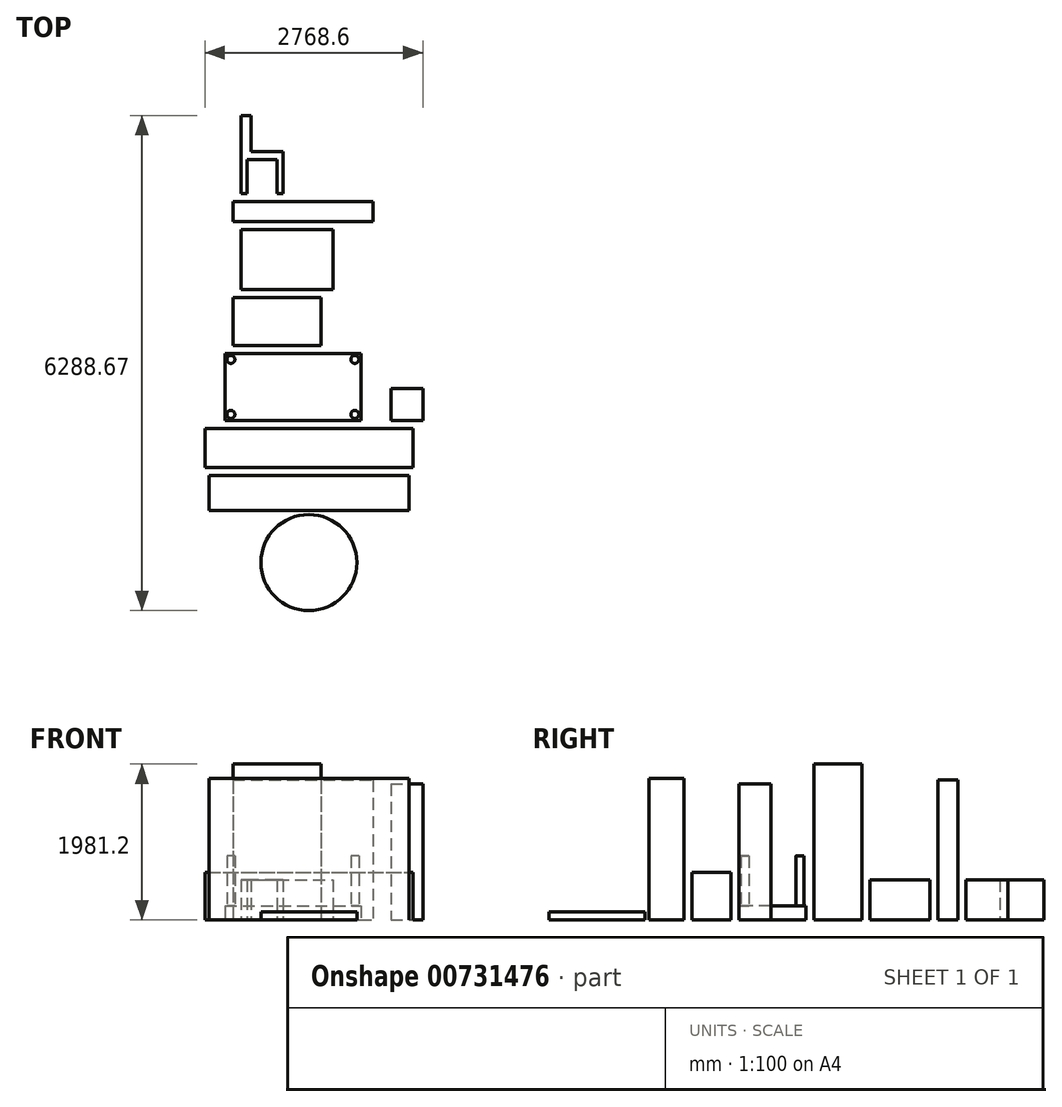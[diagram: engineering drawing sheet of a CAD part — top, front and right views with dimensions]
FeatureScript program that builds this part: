
annotation { "Feature Type Name" : "Feature", "Feature Type Description" : "" }
export const myFeature = defineFeature(function(context is Context, id is Id, definition is map)
    precondition{}
    {
        {
            var Q0;
            Q0=qCreatedBy(makeId("Top.planeOp"),FACE);
            var sketch = newSketch(context, id + "F0", { "sketchPlane" : qUnion([Q0])});
            skLineSegment(sketch, "E0.bottom", {"start": v(-1320.8, 50.8) * mm, "end": v(1320.8, 50.8) * mm});
            skLineSegment(sketch, "E0.top", {"start": v(-1320.8, 546.1) * mm, "end": v(1320.8, 546.1) * mm});
            skLineSegment(sketch, "E0.left", {"start": v(-1320.8, 50.8) * mm, "end": v(-1320.8, 546.1) * mm});
            skLineSegment(sketch, "E0.right", {"start": v(1320.8, 50.8) * mm, "end": v(1320.8, 546.1) * mm});
            skLineSegment(sketch, "E1.bottom", {"start": v(-1270, -50.8) * mm, "end": v(1270, -50.8) * mm});
            skLineSegment(sketch, "E1.top", {"start": v(-1270, -495.3) * mm, "end": v(1270, -495.3) * mm});
            skLineSegment(sketch, "E1.left", {"start": v(-1270, -50.8) * mm, "end": v(-1270, -495.3) * mm});
            skLineSegment(sketch, "E1.right", {"start": v(1270, -50.8) * mm, "end": v(1270, -495.3) * mm});
            skLineSegment(sketch, "E2", {"start": v(0, 50.8) * mm, "end": v(0, -50.8) * mm});
            skLineSegment(sketch, "E3.bottom", {"start": v(-1066.8, 1498.6) * mm, "end": v(660.4, 1498.6) * mm});
            skLineSegment(sketch, "E3.top", {"start": v(-1066.8, 647.7) * mm, "end": v(660.4, 647.7) * mm});
            skLineSegment(sketch, "E3.left", {"start": v(-1066.8, 1498.6) * mm, "end": v(-1066.8, 647.7) * mm});
            skLineSegment(sketch, "E3.right", {"start": v(660.4, 1498.6) * mm, "end": v(660.4, 647.7) * mm});
            skCircle(sketch, "E4", {"center": v(-990.6, 723.9) * mm, "radius": 50.8 * mm});
            skCircle(sketch, "E5", {"center": v(-990.6, 1422.4) * mm, "radius": 50.8 * mm});
            skCircle(sketch, "E6", {"center": v(584.2, 1422.4) * mm, "radius": 50.8 * mm});
            skCircle(sketch, "E7", {"center": v(584.2, 723.9) * mm, "radius": 50.8 * mm});
            skLineSegment(sketch, "E8.0", {"start": v(-990.6, 1422.4) * mm, "end": v(584.2, 1422.4) * mm, "construction": true});
            skLineSegment(sketch, "E8.1", {"start": v(-990.6, 1422.4) * mm, "end": v(-990.6, 723.9) * mm, "construction": true});
            skLineSegment(sketch, "E8.2", {"start": v(-990.6, 723.9) * mm, "end": v(584.2, 723.9) * mm, "construction": true});
            skLineSegment(sketch, "E8.3", {"start": v(584.2, 1422.4) * mm, "end": v(584.2, 723.9) * mm, "construction": true});
            skLineSegment(sketch, "E9.bottom", {"start": v(-965.2, 1600.2) * mm, "end": v(152.4, 1600.2) * mm});
            skLineSegment(sketch, "E9.top", {"start": v(-965.2, 2209.8) * mm, "end": v(152.4, 2209.8) * mm});
            skLineSegment(sketch, "E9.left", {"start": v(-965.2, 1600.2) * mm, "end": v(-965.2, 2209.8) * mm});
            skLineSegment(sketch, "E9.right", {"start": v(152.4, 1600.2) * mm, "end": v(152.4, 2209.8) * mm});
            skLineSegment(sketch, "E10.bottom", {"start": v(-863.6, 2311.4) * mm, "end": v(304.8, 2311.4) * mm});
            skLineSegment(sketch, "E10.top", {"start": v(-863.6, 3073.4) * mm, "end": v(304.8, 3073.4) * mm});
            skLineSegment(sketch, "E10.left", {"start": v(-863.6, 2311.4) * mm, "end": v(-863.6, 3073.4) * mm});
            skLineSegment(sketch, "E10.right", {"start": v(304.8, 2311.4) * mm, "end": v(304.8, 3073.4) * mm});
            skLineSegment(sketch, "E11.bottom", {"start": v(-965.2, 3175) * mm, "end": v(812.8, 3175) * mm});
            skLineSegment(sketch, "E11.top", {"start": v(-965.2, 3429) * mm, "end": v(812.8, 3429) * mm});
            skLineSegment(sketch, "E11.left", {"start": v(-965.2, 3175) * mm, "end": v(-965.2, 3429) * mm});
            skLineSegment(sketch, "E11.right", {"start": v(812.8, 3175) * mm, "end": v(812.8, 3429) * mm});
            skLineSegment(sketch, "E12", {"start": v(-863.6, 3530.6) * mm, "end": v(-863.6, 4521.2) * mm});
            skLineSegment(sketch, "E13", {"start": v(-863.6, 4521.2) * mm, "end": v(-736.6, 4521.2) * mm});
            skLineSegment(sketch, "E14", {"start": v(-736.6, 4521.2) * mm, "end": v(-736.6, 4064) * mm});
            skLineSegment(sketch, "E15", {"start": v(-736.6, 4064) * mm, "end": v(-330.2, 4064) * mm});
            skLineSegment(sketch, "E16", {"start": v(-330.2, 4064) * mm, "end": v(-330.2, 3530.6) * mm});
            skLineSegment(sketch, "E17", {"start": v(-330.2, 3530.6) * mm, "end": v(-406.4, 3530.6) * mm});
            skLineSegment(sketch, "E18", {"start": v(-406.4, 3530.6) * mm, "end": v(-406.4, 3962.4) * mm});
            skLineSegment(sketch, "E19", {"start": v(-406.4, 3962.4) * mm, "end": v(-787.4, 3962.4) * mm});
            skLineSegment(sketch, "E20", {"start": v(-787.4, 3962.4) * mm, "end": v(-787.4, 3530.6) * mm});
            skLineSegment(sketch, "E21", {"start": v(-787.4, 3530.6) * mm, "end": v(-863.6, 3530.6) * mm});
            skLineSegment(sketch, "E22.bottom", {"start": v(1041.4, 647.7) * mm, "end": v(1447.8, 647.7) * mm});
            skLineSegment(sketch, "E22.top", {"start": v(1041.4, 1054.1) * mm, "end": v(1447.8, 1054.1) * mm});
            skLineSegment(sketch, "E22.left", {"start": v(1041.4, 647.7) * mm, "end": v(1041.4, 1054.1) * mm});
            skLineSegment(sketch, "E22.right", {"start": v(1447.8, 647.7) * mm, "end": v(1447.8, 1054.1) * mm});
            skCircle(sketch, "E23", {"center": v(0, -1157.87) * mm, "radius": 609.6 * mm});
            skSolve(sketch);
        }
        {
            var Q0;
            Q0=makeQuery(id+"F0.imprint","IMPRINT",FACE,{"disambiguationData":[TD([[makeQuery(id+"F0.imprint","IMPRINT",EDGE,{"derivedFrom":sQuery(id+"F0.wireOp",EDGE,"E0.top")}),-1.0]])]});
            extrude(context, id + "F1", {"entities" : qUnion([Q0]), "depth" : 603.25 * mm, "offsetDistance" : 25.4 * mm});
        }
        {
            var Q0;
            Q0=makeQuery(id+"F0.imprint","IMPRINT",FACE,{"disambiguationData":[TD([[makeQuery(id+"F0.imprint","IMPRINT",EDGE,{"derivedFrom":sQuery(id+"F0.wireOp",EDGE,"E1.top")}),1.0]])]});
            extrude(context, id + "F2", {"entities" : qUnion([Q0]), "depth" : 1797.05 * mm, "offsetDistance" : 25.4 * mm});
        }
        {
            var Q0;
            Q0=makeQuery(id+"F0.imprint","IMPRINT",FACE,{"disambiguationData":[TD([[makeQuery(id+"F0.imprint","IMPRINT",EDGE,{"derivedFrom":sQuery(id+"F0.wireOp",EDGE,"E3.bottom")}),-1.0]])]});
            extrude(context, id + "F3", {"entities" : qUnion([Q0]), "depth" : 177.8 * mm, "offsetDistance" : 25.4 * mm});
        }
        {
            var Q0;
            Q0=makeQuery(id+"F0.imprint","IMPRINT",FACE,{"disambiguationData":[TD([[makeQuery(id+"F0.imprint","IMPRINT",EDGE,{"derivedFrom":sQuery(id+"F0.wireOp",EDGE,"E5")}),1.0]])]});
            var Q1;
            Q1=makeQuery(id+"F0.imprint","IMPRINT",FACE,{"disambiguationData":[TD([[makeQuery(id+"F0.imprint","IMPRINT",EDGE,{"derivedFrom":sQuery(id+"F0.wireOp",EDGE,"E6")}),1.0]])]});
            var Q2;
            Q2=makeQuery(id+"F0.imprint","IMPRINT",FACE,{"disambiguationData":[TD([[makeQuery(id+"F0.imprint","IMPRINT",EDGE,{"derivedFrom":sQuery(id+"F0.wireOp",EDGE,"E4")}),1.0]])]});
            var Q3;
            Q3=makeQuery(id+"F0.imprint","IMPRINT",FACE,{"disambiguationData":[TD([[makeQuery(id+"F0.imprint","IMPRINT",EDGE,{"derivedFrom":sQuery(id+"F0.wireOp",EDGE,"E7")}),1.0]])]});
            extrude(context, id + "F4", {"entities" : qUnion([Q0, Q1, Q2, Q3]), "operationType" : NewBodyOperationType.ADD, "depth" : 812.8 * mm, "offsetDistance" : 25.4 * mm});
        }
        {
            var Q0;
            Q0=makeQuery(id+"F0.imprint","IMPRINT",FACE,{"disambiguationData":[TD([[makeQuery(id+"F0.imprint","IMPRINT",EDGE,{"derivedFrom":sQuery(id+"F0.wireOp",EDGE,"E9.bottom")}),1.0]])]});
            extrude(context, id + "F5", {"entities" : qUnion([Q0]), "depth" : 1981.2 * mm, "offsetDistance" : 25.4 * mm});
        }
        {
            var Q0;
            Q0=makeQuery(id+"F0.imprint","IMPRINT",FACE,{"disambiguationData":[TD([[makeQuery(id+"F0.imprint","IMPRINT",EDGE,{"derivedFrom":sQuery(id+"F0.wireOp",EDGE,"E10.bottom")}),1.0]])]});
            extrude(context, id + "F6", {"entities" : qUnion([Q0]), "depth" : 508 * mm, "offsetDistance" : 25.4 * mm});
        }
        {
            var Q0;
            Q0=makeQuery(id+"F0.imprint","IMPRINT",FACE,{"disambiguationData":[TD([[makeQuery(id+"F0.imprint","IMPRINT",EDGE,{"derivedFrom":sQuery(id+"F0.wireOp",EDGE,"E11.bottom")}),1.0]])]});
            extrude(context, id + "F7", {"entities" : qUnion([Q0]), "depth" : 1778 * mm, "offsetDistance" : 25.4 * mm});
        }
        {
            var Q0;
            Q0=makeQuery(id+"F0.imprint","IMPRINT",FACE,{"disambiguationData":[TD([[makeQuery(id+"F0.imprint","IMPRINT",EDGE,{"derivedFrom":sQuery(id+"F0.wireOp",EDGE,"E12")}),-1.0]])]});
            extrude(context, id + "F8", {"entities" : qUnion([Q0]), "depth" : 508 * mm, "offsetDistance" : 25.4 * mm});
        }
        {
            var Q0;
            Q0=makeQuery(id+"F0.imprint","IMPRINT",FACE,{"disambiguationData":[TD([[makeQuery(id+"F0.imprint","IMPRINT",EDGE,{"derivedFrom":sQuery(id+"F0.wireOp",EDGE,"E22.bottom")}),1.0]])]});
            extrude(context, id + "F9", {"entities" : qUnion([Q0]), "depth" : 1727.2 * mm, "offsetDistance" : 25.4 * mm});
        }
        {
            var Q0;
            Q0=makeQuery(id+"F0.imprint","IMPRINT",FACE,{"disambiguationData":[TD([[makeQuery(id+"F0.imprint","IMPRINT",EDGE,{"derivedFrom":sQuery(id+"F0.wireOp",EDGE,"E23")}),1.0]])]});
            extrude(context, id + "F10", {"entities" : qUnion([Q0]), "depth" : 101.6 * mm, "offsetDistance" : 25.4 * mm});
        }
    });
